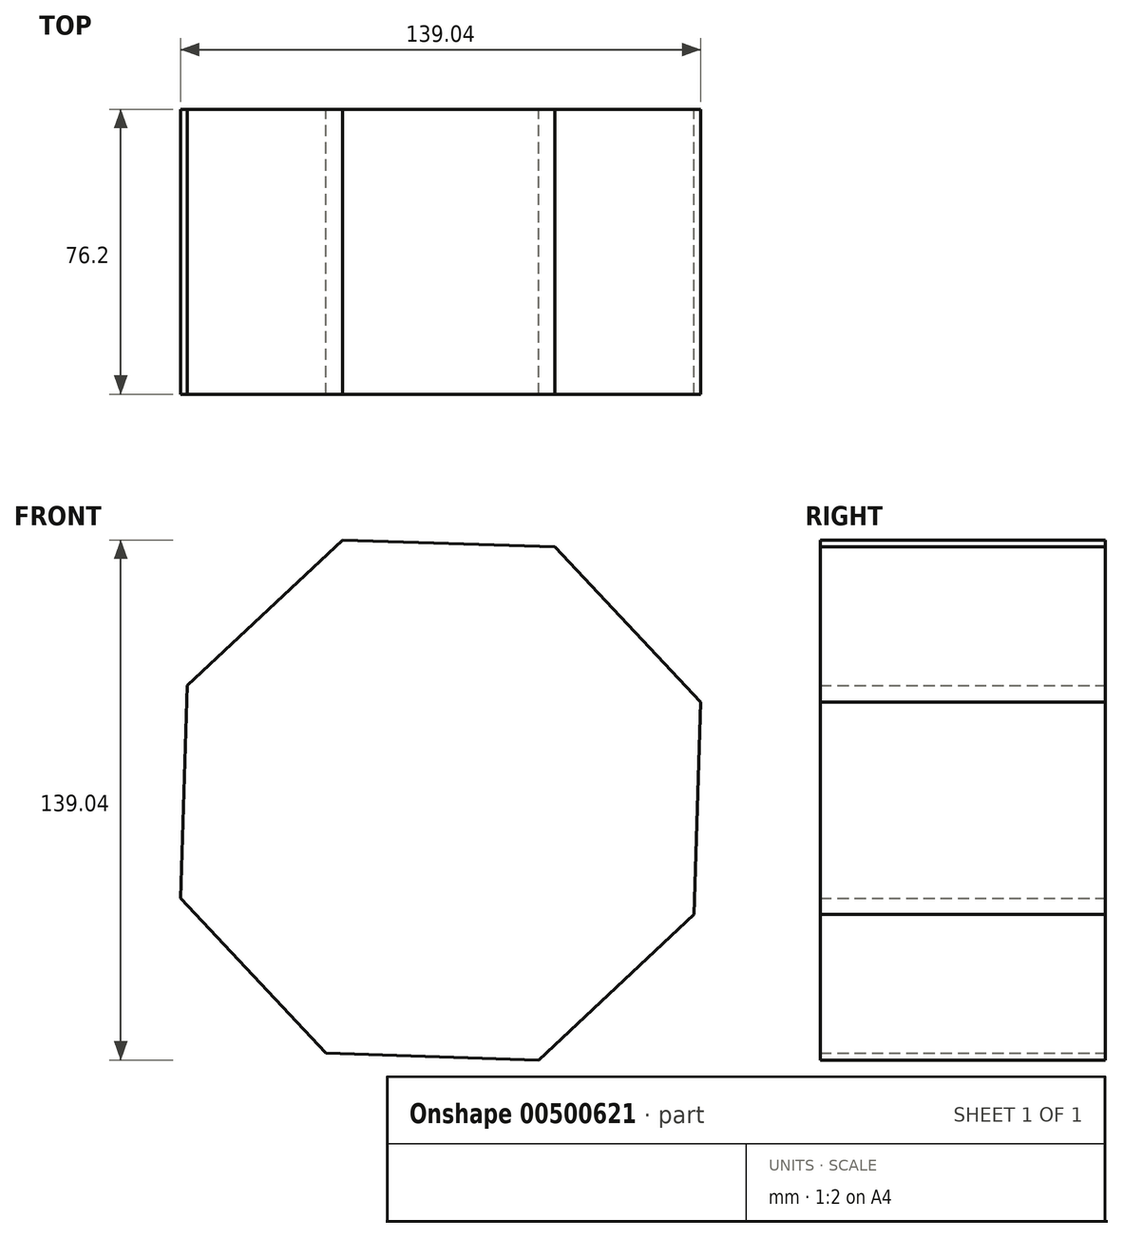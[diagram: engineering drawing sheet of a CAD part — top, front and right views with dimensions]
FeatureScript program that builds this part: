
annotation { "Feature Type Name" : "Feature", "Feature Type Description" : "" }
export const myFeature = defineFeature(function(context is Context, id is Id, definition is map)
    precondition{}
    {
        {
            var Q0;
            Q0=qCreatedBy(makeId("Front.planeOp"),FACE);
            var sketch = newSketch(context, id + "F0", { "sketchPlane" : qUnion([Q0])});
            skCircle(sketch, "E0.cCircle", {"center": v(0, 0) * mm, "radius": 74.3 * mm, "construction": true});
            skLineSegment(sketch, "E0.0", {"start": v(30.6, 67.7) * mm, "end": v(69.52, 26.23) * mm});
            skLineSegment(sketch, "E0.1", {"start": v(69.52, 26.23) * mm, "end": v(67.7, -30.6) * mm});
            skLineSegment(sketch, "E0.2", {"start": v(67.7, -30.6) * mm, "end": v(26.23, -69.52) * mm});
            skLineSegment(sketch, "E0.3", {"start": v(26.23, -69.52) * mm, "end": v(-30.6, -67.7) * mm});
            skLineSegment(sketch, "E0.4", {"start": v(-30.6, -67.7) * mm, "end": v(-69.52, -26.23) * mm});
            skLineSegment(sketch, "E0.5", {"start": v(-69.52, -26.23) * mm, "end": v(-67.7, 30.6) * mm});
            skLineSegment(sketch, "E0.6", {"start": v(-67.7, 30.6) * mm, "end": v(-26.23, 69.52) * mm});
            skLineSegment(sketch, "E0.7", {"start": v(-26.23, 69.52) * mm, "end": v(30.6, 67.7) * mm});
            skSolve(sketch);
        }
        {
            var Q0;
            Q0 = qSketchRegion(id + "F0", true);
            extrude(context, id + "F1", {"entities" : qUnion([Q0]), "depth" : 76.2 * mm});
        }
    });
